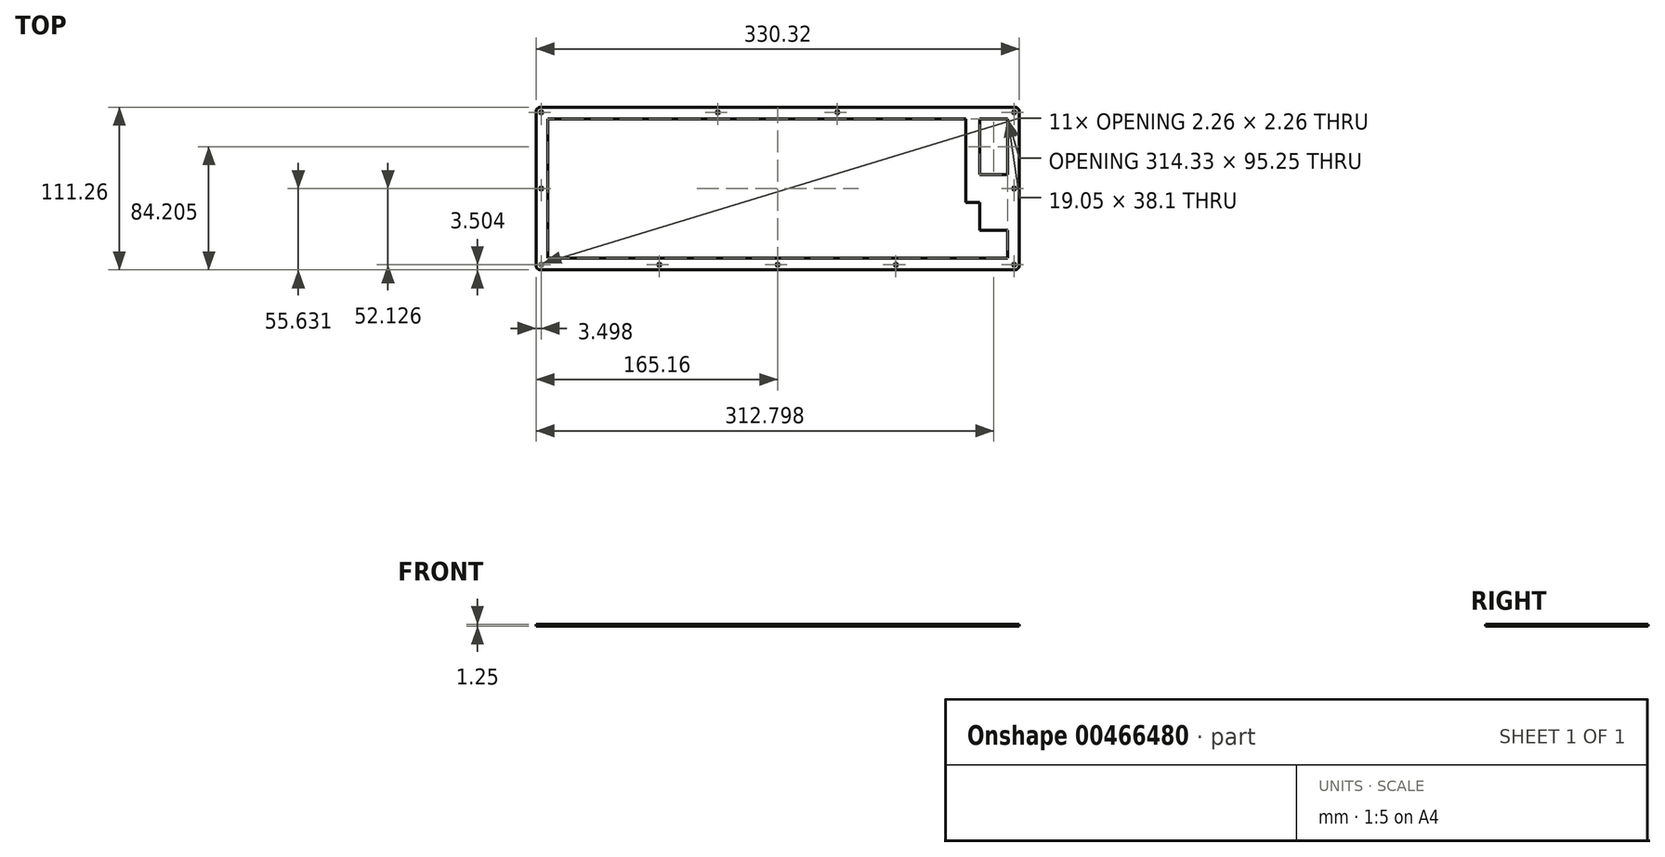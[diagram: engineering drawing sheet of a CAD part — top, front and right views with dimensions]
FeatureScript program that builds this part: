
annotation { "Feature Type Name" : "Feature", "Feature Type Description" : "" }
export const myFeature = defineFeature(function(context is Context, id is Id, definition is map)
    precondition{}
    {
        {
            var Q0;
            Q0=qCreatedBy(makeId("Top.planeOp"),FACE);
            var sketch = newSketch(context, id + "F0", { "sketchPlane" : qUnion([Q0])});
            skLineSegment(sketch, "E0", {"start": v(162.16, 55.62) * mm, "end": v(162.4, 55.62) * mm});
            skLineSegment(sketch, "E1", {"start": v(162.4, 55.62) * mm, "end": v(162.63, 55.59) * mm});
            skLineSegment(sketch, "E2", {"start": v(162.63, 55.59) * mm, "end": v(162.86, 55.54) * mm});
            skLineSegment(sketch, "E3", {"start": v(162.86, 55.54) * mm, "end": v(163.1, 55.48) * mm});
            skLineSegment(sketch, "E4", {"start": v(163.1, 55.48) * mm, "end": v(163.31, 55.4) * mm});
            skLineSegment(sketch, "E5", {"start": v(163.31, 55.4) * mm, "end": v(163.53, 55.3) * mm});
            skLineSegment(sketch, "E6", {"start": v(163.53, 55.3) * mm, "end": v(163.73, 55.18) * mm});
            skLineSegment(sketch, "E7", {"start": v(163.73, 55.18) * mm, "end": v(163.93, 55.05) * mm});
            skLineSegment(sketch, "E8", {"start": v(163.93, 55.05) * mm, "end": v(164.11, 54.9) * mm});
            skLineSegment(sketch, "E9", {"start": v(164.11, 54.9) * mm, "end": v(164.29, 54.75) * mm});
            skLineSegment(sketch, "E10", {"start": v(164.29, 54.75) * mm, "end": v(164.45, 54.57) * mm});
            skLineSegment(sketch, "E11", {"start": v(164.45, 54.57) * mm, "end": v(164.6, 54.39) * mm});
            skLineSegment(sketch, "E12", {"start": v(164.6, 54.39) * mm, "end": v(164.72, 54.2) * mm});
            skLineSegment(sketch, "E13", {"start": v(164.72, 54.2) * mm, "end": v(164.84, 53.99) * mm});
            skLineSegment(sketch, "E14", {"start": v(164.84, 53.99) * mm, "end": v(164.93, 53.77) * mm});
            skLineSegment(sketch, "E15", {"start": v(164.93, 53.77) * mm, "end": v(165.02, 53.55) * mm});
            skLineSegment(sketch, "E16", {"start": v(165.02, 53.55) * mm, "end": v(165.08, 53.33) * mm});
            skLineSegment(sketch, "E17", {"start": v(165.08, 53.33) * mm, "end": v(165.13, 53.1) * mm});
            skLineSegment(sketch, "E18", {"start": v(165.13, 53.1) * mm, "end": v(165.15, 52.86) * mm});
            skLineSegment(sketch, "E19", {"start": v(165.15, 52.86) * mm, "end": v(165.16, 52.62) * mm});
            skLineSegment(sketch, "E20", {"start": v(165.16, 52.62) * mm, "end": v(165.16, -52.63) * mm});
            skLineSegment(sketch, "E21", {"start": v(165.16, -52.63) * mm, "end": v(165.15, -52.86) * mm});
            skLineSegment(sketch, "E22", {"start": v(165.15, -52.86) * mm, "end": v(165.13, -53.1) * mm});
            skLineSegment(sketch, "E23", {"start": v(165.13, -53.1) * mm, "end": v(165.08, -53.33) * mm});
            skLineSegment(sketch, "E24", {"start": v(165.08, -53.33) * mm, "end": v(165.02, -53.55) * mm});
            skLineSegment(sketch, "E25", {"start": v(165.02, -53.55) * mm, "end": v(164.93, -53.77) * mm});
            skLineSegment(sketch, "E26", {"start": v(164.93, -53.77) * mm, "end": v(164.84, -53.99) * mm});
            skLineSegment(sketch, "E27", {"start": v(164.84, -53.99) * mm, "end": v(164.72, -54.2) * mm});
            skLineSegment(sketch, "E28", {"start": v(164.72, -54.2) * mm, "end": v(164.6, -54.39) * mm});
            skLineSegment(sketch, "E29", {"start": v(164.6, -54.39) * mm, "end": v(164.45, -54.57) * mm});
            skLineSegment(sketch, "E30", {"start": v(164.45, -54.57) * mm, "end": v(164.29, -54.75) * mm});
            skLineSegment(sketch, "E31", {"start": v(164.29, -54.75) * mm, "end": v(164.11, -54.9) * mm});
            skLineSegment(sketch, "E32", {"start": v(164.11, -54.9) * mm, "end": v(163.93, -55.05) * mm});
            skLineSegment(sketch, "E33", {"start": v(163.93, -55.05) * mm, "end": v(163.73, -55.18) * mm});
            skLineSegment(sketch, "E34", {"start": v(163.73, -55.18) * mm, "end": v(163.53, -55.3) * mm});
            skLineSegment(sketch, "E35", {"start": v(163.53, -55.3) * mm, "end": v(163.31, -55.4) * mm});
            skLineSegment(sketch, "E36", {"start": v(163.31, -55.4) * mm, "end": v(163.1, -55.48) * mm});
            skLineSegment(sketch, "E37", {"start": v(163.1, -55.48) * mm, "end": v(162.86, -55.54) * mm});
            skLineSegment(sketch, "E38", {"start": v(162.86, -55.54) * mm, "end": v(162.63, -55.59) * mm});
            skLineSegment(sketch, "E39", {"start": v(162.63, -55.59) * mm, "end": v(162.4, -55.62) * mm});
            skLineSegment(sketch, "E40", {"start": v(162.4, -55.62) * mm, "end": v(162.16, -55.63) * mm});
            skLineSegment(sketch, "E41", {"start": v(162.16, -55.63) * mm, "end": v(-162.16, -55.63) * mm});
            skLineSegment(sketch, "E42", {"start": v(-162.16, -55.63) * mm, "end": v(-162.4, -55.62) * mm});
            skLineSegment(sketch, "E43", {"start": v(-162.4, -55.62) * mm, "end": v(-162.63, -55.59) * mm});
            skLineSegment(sketch, "E44", {"start": v(-162.63, -55.59) * mm, "end": v(-162.86, -55.54) * mm});
            skLineSegment(sketch, "E45", {"start": v(-162.86, -55.54) * mm, "end": v(-163.09, -55.48) * mm});
            skLineSegment(sketch, "E46", {"start": v(-163.09, -55.48) * mm, "end": v(-163.31, -55.4) * mm});
            skLineSegment(sketch, "E47", {"start": v(-163.31, -55.4) * mm, "end": v(-163.52, -55.3) * mm});
            skLineSegment(sketch, "E48", {"start": v(-163.52, -55.3) * mm, "end": v(-163.73, -55.18) * mm});
            skLineSegment(sketch, "E49", {"start": v(-163.73, -55.18) * mm, "end": v(-163.93, -55.05) * mm});
            skLineSegment(sketch, "E50", {"start": v(-163.93, -55.05) * mm, "end": v(-164.11, -54.9) * mm});
            skLineSegment(sketch, "E51", {"start": v(-164.11, -54.9) * mm, "end": v(-164.28, -54.75) * mm});
            skLineSegment(sketch, "E52", {"start": v(-164.28, -54.75) * mm, "end": v(-164.44, -54.57) * mm});
            skLineSegment(sketch, "E53", {"start": v(-164.44, -54.57) * mm, "end": v(-164.6, -54.39) * mm});
            skLineSegment(sketch, "E54", {"start": v(-164.6, -54.39) * mm, "end": v(-164.72, -54.2) * mm});
            skLineSegment(sketch, "E55", {"start": v(-164.72, -54.2) * mm, "end": v(-164.84, -53.99) * mm});
            skLineSegment(sketch, "E56", {"start": v(-164.84, -53.99) * mm, "end": v(-164.93, -53.77) * mm});
            skLineSegment(sketch, "E57", {"start": v(-164.93, -53.77) * mm, "end": v(-165.02, -53.55) * mm});
            skLineSegment(sketch, "E58", {"start": v(-165.02, -53.55) * mm, "end": v(-165.08, -53.33) * mm});
            skLineSegment(sketch, "E59", {"start": v(-165.08, -53.33) * mm, "end": v(-165.13, -53.1) * mm});
            skLineSegment(sketch, "E60", {"start": v(-165.13, -53.1) * mm, "end": v(-165.15, -52.86) * mm});
            skLineSegment(sketch, "E61", {"start": v(-165.15, -52.86) * mm, "end": v(-165.16, -52.63) * mm});
            skLineSegment(sketch, "E62", {"start": v(-165.16, -52.63) * mm, "end": v(-165.16, 52.62) * mm});
            skLineSegment(sketch, "E63", {"start": v(-165.16, 52.62) * mm, "end": v(-165.15, 52.86) * mm});
            skLineSegment(sketch, "E64", {"start": v(-165.15, 52.86) * mm, "end": v(-165.13, 53.1) * mm});
            skLineSegment(sketch, "E65", {"start": v(-165.13, 53.1) * mm, "end": v(-165.08, 53.33) * mm});
            skLineSegment(sketch, "E66", {"start": v(-165.08, 53.33) * mm, "end": v(-165.02, 53.55) * mm});
            skLineSegment(sketch, "E67", {"start": v(-165.02, 53.55) * mm, "end": v(-164.93, 53.77) * mm});
            skLineSegment(sketch, "E68", {"start": v(-164.93, 53.77) * mm, "end": v(-164.84, 53.99) * mm});
            skLineSegment(sketch, "E69", {"start": v(-164.84, 53.99) * mm, "end": v(-164.72, 54.2) * mm});
            skLineSegment(sketch, "E70", {"start": v(-164.72, 54.2) * mm, "end": v(-164.6, 54.39) * mm});
            skLineSegment(sketch, "E71", {"start": v(-164.6, 54.39) * mm, "end": v(-164.44, 54.57) * mm});
            skLineSegment(sketch, "E72", {"start": v(-164.44, 54.57) * mm, "end": v(-164.28, 54.75) * mm});
            skLineSegment(sketch, "E73", {"start": v(-164.28, 54.75) * mm, "end": v(-164.11, 54.9) * mm});
            skLineSegment(sketch, "E74", {"start": v(-164.11, 54.9) * mm, "end": v(-163.93, 55.05) * mm});
            skLineSegment(sketch, "E75", {"start": v(-163.93, 55.05) * mm, "end": v(-163.73, 55.18) * mm});
            skLineSegment(sketch, "E76", {"start": v(-163.73, 55.18) * mm, "end": v(-163.52, 55.3) * mm});
            skLineSegment(sketch, "E77", {"start": v(-163.52, 55.3) * mm, "end": v(-163.31, 55.4) * mm});
            skLineSegment(sketch, "E78", {"start": v(-163.31, 55.4) * mm, "end": v(-163.09, 55.48) * mm});
            skLineSegment(sketch, "E79", {"start": v(-163.09, 55.48) * mm, "end": v(-162.86, 55.54) * mm});
            skLineSegment(sketch, "E80", {"start": v(-162.86, 55.54) * mm, "end": v(-162.63, 55.59) * mm});
            skLineSegment(sketch, "E81", {"start": v(-162.63, 55.59) * mm, "end": v(-162.4, 55.62) * mm});
            skLineSegment(sketch, "E82", {"start": v(-162.4, 55.62) * mm, "end": v(-162.16, 55.63) * mm});
            skLineSegment(sketch, "E83", {"start": v(-162.16, 55.63) * mm, "end": v(162.16, 55.62) * mm});
            skLineSegment(sketch, "E84", {"start": v(161.31, -51.05) * mm, "end": v(161, -51.21) * mm});
            skLineSegment(sketch, "E85", {"start": v(161, -51.21) * mm, "end": v(160.75, -51.46) * mm});
            skLineSegment(sketch, "E86", {"start": v(160.75, -51.46) * mm, "end": v(160.59, -51.78) * mm});
            skLineSegment(sketch, "E87", {"start": v(160.59, -51.78) * mm, "end": v(160.53, -52.13) * mm});
            skLineSegment(sketch, "E88", {"start": v(160.53, -52.13) * mm, "end": v(160.59, -52.48) * mm});
            skLineSegment(sketch, "E89", {"start": v(160.59, -52.48) * mm, "end": v(160.75, -52.79) * mm});
            skLineSegment(sketch, "E90", {"start": v(160.75, -52.79) * mm, "end": v(161, -53.04) * mm});
            skLineSegment(sketch, "E91", {"start": v(161, -53.04) * mm, "end": v(161.31, -53.2) * mm});
            skLineSegment(sketch, "E92", {"start": v(161.31, -53.2) * mm, "end": v(161.66, -53.26) * mm});
            skLineSegment(sketch, "E93", {"start": v(161.66, -53.26) * mm, "end": v(162.01, -53.2) * mm});
            skLineSegment(sketch, "E94", {"start": v(162.01, -53.2) * mm, "end": v(162.33, -53.04) * mm});
            skLineSegment(sketch, "E95", {"start": v(162.33, -53.04) * mm, "end": v(162.58, -52.79) * mm});
            skLineSegment(sketch, "E96", {"start": v(162.58, -52.79) * mm, "end": v(162.74, -52.48) * mm});
            skLineSegment(sketch, "E97", {"start": v(162.74, -52.48) * mm, "end": v(162.8, -52.13) * mm});
            skLineSegment(sketch, "E98", {"start": v(162.8, -52.13) * mm, "end": v(162.74, -51.78) * mm});
            skLineSegment(sketch, "E99", {"start": v(162.74, -51.78) * mm, "end": v(162.58, -51.46) * mm});
            skLineSegment(sketch, "E100", {"start": v(162.58, -51.46) * mm, "end": v(162.33, -51.21) * mm});
            skLineSegment(sketch, "E101", {"start": v(162.33, -51.21) * mm, "end": v(162.01, -51.05) * mm});
            skLineSegment(sketch, "E102", {"start": v(162.01, -51.05) * mm, "end": v(161.66, -51) * mm});
            skLineSegment(sketch, "E103", {"start": v(161.66, -51) * mm, "end": v(161.31, -51.05) * mm});
            skLineSegment(sketch, "E104", {"start": v(80.48, -51.05) * mm, "end": v(80.17, -51.21) * mm});
            skLineSegment(sketch, "E105", {"start": v(80.17, -51.21) * mm, "end": v(79.92, -51.46) * mm});
            skLineSegment(sketch, "E106", {"start": v(79.92, -51.46) * mm, "end": v(79.76, -51.78) * mm});
            skLineSegment(sketch, "E107", {"start": v(79.76, -51.78) * mm, "end": v(79.7, -52.13) * mm});
            skLineSegment(sketch, "E108", {"start": v(79.7, -52.13) * mm, "end": v(79.76, -52.48) * mm});
            skLineSegment(sketch, "E109", {"start": v(79.76, -52.48) * mm, "end": v(79.92, -52.79) * mm});
            skLineSegment(sketch, "E110", {"start": v(79.92, -52.79) * mm, "end": v(80.17, -53.04) * mm});
            skLineSegment(sketch, "E111", {"start": v(80.17, -53.04) * mm, "end": v(80.48, -53.2) * mm});
            skLineSegment(sketch, "E112", {"start": v(80.48, -53.2) * mm, "end": v(80.83, -53.26) * mm});
            skLineSegment(sketch, "E113", {"start": v(80.83, -53.26) * mm, "end": v(81.18, -53.2) * mm});
            skLineSegment(sketch, "E114", {"start": v(81.18, -53.2) * mm, "end": v(81.5, -53.04) * mm});
            skLineSegment(sketch, "E115", {"start": v(81.5, -53.04) * mm, "end": v(81.75, -52.79) * mm});
            skLineSegment(sketch, "E116", {"start": v(81.75, -52.79) * mm, "end": v(81.9, -52.48) * mm});
            skLineSegment(sketch, "E117", {"start": v(81.9, -52.48) * mm, "end": v(81.96, -52.13) * mm});
            skLineSegment(sketch, "E118", {"start": v(81.96, -52.13) * mm, "end": v(81.9, -51.78) * mm});
            skLineSegment(sketch, "E119", {"start": v(81.9, -51.78) * mm, "end": v(81.75, -51.46) * mm});
            skLineSegment(sketch, "E120", {"start": v(81.75, -51.46) * mm, "end": v(81.5, -51.21) * mm});
            skLineSegment(sketch, "E121", {"start": v(81.5, -51.21) * mm, "end": v(81.18, -51.05) * mm});
            skLineSegment(sketch, "E122", {"start": v(81.18, -51.05) * mm, "end": v(80.83, -51) * mm});
            skLineSegment(sketch, "E123", {"start": v(80.83, -51) * mm, "end": v(80.48, -51.05) * mm});
            skLineSegment(sketch, "E124", {"start": v(-0.35, -51.05) * mm, "end": v(-0.66, -51.21) * mm});
            skLineSegment(sketch, "E125", {"start": v(-0.66, -51.21) * mm, "end": v(-0.91, -51.46) * mm});
            skLineSegment(sketch, "E126", {"start": v(-0.91, -51.46) * mm, "end": v(-1.07, -51.78) * mm});
            skLineSegment(sketch, "E127", {"start": v(-1.07, -51.78) * mm, "end": v(-1.13, -52.13) * mm});
            skLineSegment(sketch, "E128", {"start": v(-1.13, -52.13) * mm, "end": v(-1.07, -52.48) * mm});
            skLineSegment(sketch, "E129", {"start": v(-1.07, -52.48) * mm, "end": v(-0.91, -52.79) * mm});
            skLineSegment(sketch, "E130", {"start": v(-0.91, -52.79) * mm, "end": v(-0.66, -53.04) * mm});
            skLineSegment(sketch, "E131", {"start": v(-0.66, -53.04) * mm, "end": v(-0.35, -53.2) * mm});
            skLineSegment(sketch, "E132", {"start": v(-0.35, -53.2) * mm, "end": v(0, -53.26) * mm});
            skLineSegment(sketch, "E133", {"start": v(0, -53.26) * mm, "end": v(0.35, -53.2) * mm});
            skLineSegment(sketch, "E134", {"start": v(0.35, -53.2) * mm, "end": v(0.67, -53.04) * mm});
            skLineSegment(sketch, "E135", {"start": v(0.67, -53.04) * mm, "end": v(0.92, -52.79) * mm});
            skLineSegment(sketch, "E136", {"start": v(0.92, -52.79) * mm, "end": v(1.07, -52.48) * mm});
            skLineSegment(sketch, "E137", {"start": v(1.07, -52.48) * mm, "end": v(1.13, -52.13) * mm});
            skLineSegment(sketch, "E138", {"start": v(1.13, -52.13) * mm, "end": v(1.07, -51.78) * mm});
            skLineSegment(sketch, "E139", {"start": v(1.07, -51.78) * mm, "end": v(0.92, -51.46) * mm});
            skLineSegment(sketch, "E140", {"start": v(0.92, -51.46) * mm, "end": v(0.67, -51.21) * mm});
            skLineSegment(sketch, "E141", {"start": v(0.67, -51.21) * mm, "end": v(0.35, -51.05) * mm});
            skLineSegment(sketch, "E142", {"start": v(0.35, -51.05) * mm, "end": v(0, -51) * mm});
            skLineSegment(sketch, "E143", {"start": v(0, -51) * mm, "end": v(-0.35, -51.05) * mm});
            skLineSegment(sketch, "E144", {"start": v(-81.18, -51.05) * mm, "end": v(-81.5, -51.21) * mm});
            skLineSegment(sketch, "E145", {"start": v(-81.5, -51.21) * mm, "end": v(-81.75, -51.46) * mm});
            skLineSegment(sketch, "E146", {"start": v(-81.75, -51.46) * mm, "end": v(-81.9, -51.78) * mm});
            skLineSegment(sketch, "E147", {"start": v(-81.9, -51.78) * mm, "end": v(-81.96, -52.13) * mm});
            skLineSegment(sketch, "E148", {"start": v(-81.96, -52.13) * mm, "end": v(-81.9, -52.48) * mm});
            skLineSegment(sketch, "E149", {"start": v(-81.9, -52.48) * mm, "end": v(-81.75, -52.79) * mm});
            skLineSegment(sketch, "E150", {"start": v(-81.75, -52.79) * mm, "end": v(-81.5, -53.04) * mm});
            skLineSegment(sketch, "E151", {"start": v(-81.5, -53.04) * mm, "end": v(-81.18, -53.2) * mm});
            skLineSegment(sketch, "E152", {"start": v(-81.18, -53.2) * mm, "end": v(-80.83, -53.26) * mm});
            skLineSegment(sketch, "E153", {"start": v(-80.83, -53.26) * mm, "end": v(-80.48, -53.2) * mm});
            skLineSegment(sketch, "E154", {"start": v(-80.48, -53.2) * mm, "end": v(-80.17, -53.04) * mm});
            skLineSegment(sketch, "E155", {"start": v(-80.17, -53.04) * mm, "end": v(-79.92, -52.79) * mm});
            skLineSegment(sketch, "E156", {"start": v(-79.92, -52.79) * mm, "end": v(-79.76, -52.48) * mm});
            skLineSegment(sketch, "E157", {"start": v(-79.76, -52.48) * mm, "end": v(-79.7, -52.13) * mm});
            skLineSegment(sketch, "E158", {"start": v(-79.7, -52.13) * mm, "end": v(-79.76, -51.78) * mm});
            skLineSegment(sketch, "E159", {"start": v(-79.76, -51.78) * mm, "end": v(-79.92, -51.46) * mm});
            skLineSegment(sketch, "E160", {"start": v(-79.92, -51.46) * mm, "end": v(-80.17, -51.21) * mm});
            skLineSegment(sketch, "E161", {"start": v(-80.17, -51.21) * mm, "end": v(-80.48, -51.05) * mm});
            skLineSegment(sketch, "E162", {"start": v(-80.48, -51.05) * mm, "end": v(-80.83, -51) * mm});
            skLineSegment(sketch, "E163", {"start": v(-80.83, -51) * mm, "end": v(-81.18, -51.05) * mm});
            skLineSegment(sketch, "E164", {"start": v(-162.01, -51.05) * mm, "end": v(-162.33, -51.21) * mm});
            skLineSegment(sketch, "E165", {"start": v(-162.33, -51.21) * mm, "end": v(-162.58, -51.46) * mm});
            skLineSegment(sketch, "E166", {"start": v(-162.58, -51.46) * mm, "end": v(-162.74, -51.78) * mm});
            skLineSegment(sketch, "E167", {"start": v(-162.74, -51.78) * mm, "end": v(-162.8, -52.13) * mm});
            skLineSegment(sketch, "E168", {"start": v(-162.8, -52.13) * mm, "end": v(-162.74, -52.48) * mm});
            skLineSegment(sketch, "E169", {"start": v(-162.74, -52.48) * mm, "end": v(-162.58, -52.79) * mm});
            skLineSegment(sketch, "E170", {"start": v(-162.58, -52.79) * mm, "end": v(-162.33, -53.04) * mm});
            skLineSegment(sketch, "E171", {"start": v(-162.33, -53.04) * mm, "end": v(-162.01, -53.2) * mm});
            skLineSegment(sketch, "E172", {"start": v(-162.01, -53.2) * mm, "end": v(-161.66, -53.26) * mm});
            skLineSegment(sketch, "E173", {"start": v(-161.66, -53.26) * mm, "end": v(-161.31, -53.2) * mm});
            skLineSegment(sketch, "E174", {"start": v(-161.31, -53.2) * mm, "end": v(-161, -53.04) * mm});
            skLineSegment(sketch, "E175", {"start": v(-161, -53.04) * mm, "end": v(-160.75, -52.79) * mm});
            skLineSegment(sketch, "E176", {"start": v(-160.75, -52.79) * mm, "end": v(-160.59, -52.48) * mm});
            skLineSegment(sketch, "E177", {"start": v(-160.59, -52.48) * mm, "end": v(-160.53, -52.13) * mm});
            skLineSegment(sketch, "E178", {"start": v(-160.53, -52.13) * mm, "end": v(-160.59, -51.78) * mm});
            skLineSegment(sketch, "E179", {"start": v(-160.59, -51.78) * mm, "end": v(-160.75, -51.46) * mm});
            skLineSegment(sketch, "E180", {"start": v(-160.75, -51.46) * mm, "end": v(-161, -51.21) * mm});
            skLineSegment(sketch, "E181", {"start": v(-161, -51.21) * mm, "end": v(-161.31, -51.05) * mm});
            skLineSegment(sketch, "E182", {"start": v(-161.31, -51.05) * mm, "end": v(-161.66, -51) * mm});
            skLineSegment(sketch, "E183", {"start": v(-161.66, -51) * mm, "end": v(-162.01, -51.05) * mm});
            skLineSegment(sketch, "E184", {"start": v(-157.16, 47.63) * mm, "end": v(-157.16, 28.57) * mm});
            skLineSegment(sketch, "E185", {"start": v(-157.16, 28.57) * mm, "end": v(-157.16, 28.57) * mm});
            skLineSegment(sketch, "E186", {"start": v(-157.16, 28.57) * mm, "end": v(-157.16, 9.53) * mm});
            skLineSegment(sketch, "E187", {"start": v(-157.16, 9.53) * mm, "end": v(-157.16, 9.53) * mm});
            skLineSegment(sketch, "E188", {"start": v(-157.16, 9.53) * mm, "end": v(-157.16, -9.53) * mm});
            skLineSegment(sketch, "E189", {"start": v(-157.16, -9.53) * mm, "end": v(-157.16, -9.53) * mm});
            skLineSegment(sketch, "E190", {"start": v(-157.16, -9.53) * mm, "end": v(-157.16, -47.62) * mm});
            skLineSegment(sketch, "E191", {"start": v(-157.16, -47.62) * mm, "end": v(157.16, -47.62) * mm});
            skLineSegment(sketch, "E192", {"start": v(157.16, -47.62) * mm, "end": v(157.16, -28.57) * mm});
            skLineSegment(sketch, "E193", {"start": v(157.16, -28.57) * mm, "end": v(138.11, -28.57) * mm});
            skLineSegment(sketch, "E194", {"start": v(138.11, -28.57) * mm, "end": v(138.11, -9.52) * mm});
            skLineSegment(sketch, "E195", {"start": v(138.11, -9.52) * mm, "end": v(128.59, -9.52) * mm});
            skLineSegment(sketch, "E196", {"start": v(128.59, -9.52) * mm, "end": v(128.59, 47.63) * mm});
            skLineSegment(sketch, "E197", {"start": v(128.59, 47.63) * mm, "end": v(-157.16, 47.63) * mm});
            skLineSegment(sketch, "E198", {"start": v(161.31, 1.08) * mm, "end": v(161, 0.91) * mm});
            skLineSegment(sketch, "E199", {"start": v(161, 0.91) * mm, "end": v(160.75, 0.66) * mm});
            skLineSegment(sketch, "E200", {"start": v(160.75, 0.66) * mm, "end": v(160.59, 0.35) * mm});
            skLineSegment(sketch, "E201", {"start": v(160.59, 0.35) * mm, "end": v(160.53, 0) * mm});
            skLineSegment(sketch, "E202", {"start": v(160.53, 0) * mm, "end": v(160.59, -0.35) * mm});
            skLineSegment(sketch, "E203", {"start": v(160.59, -0.35) * mm, "end": v(160.75, -0.66) * mm});
            skLineSegment(sketch, "E204", {"start": v(160.75, -0.66) * mm, "end": v(161, -0.91) * mm});
            skLineSegment(sketch, "E205", {"start": v(161, -0.91) * mm, "end": v(161.31, -1.07) * mm});
            skLineSegment(sketch, "E206", {"start": v(161.31, -1.07) * mm, "end": v(161.66, -1.13) * mm});
            skLineSegment(sketch, "E207", {"start": v(161.66, -1.13) * mm, "end": v(162.01, -1.07) * mm});
            skLineSegment(sketch, "E208", {"start": v(162.01, -1.07) * mm, "end": v(162.33, -0.91) * mm});
            skLineSegment(sketch, "E209", {"start": v(162.33, -0.91) * mm, "end": v(162.58, -0.66) * mm});
            skLineSegment(sketch, "E210", {"start": v(162.58, -0.66) * mm, "end": v(162.74, -0.35) * mm});
            skLineSegment(sketch, "E211", {"start": v(162.74, -0.35) * mm, "end": v(162.8, 0) * mm});
            skLineSegment(sketch, "E212", {"start": v(162.8, 0) * mm, "end": v(162.74, 0.35) * mm});
            skLineSegment(sketch, "E213", {"start": v(162.74, 0.35) * mm, "end": v(162.58, 0.66) * mm});
            skLineSegment(sketch, "E214", {"start": v(162.58, 0.66) * mm, "end": v(162.33, 0.91) * mm});
            skLineSegment(sketch, "E215", {"start": v(162.33, 0.91) * mm, "end": v(162.01, 1.08) * mm});
            skLineSegment(sketch, "E216", {"start": v(162.01, 1.08) * mm, "end": v(161.66, 1.13) * mm});
            skLineSegment(sketch, "E217", {"start": v(161.66, 1.13) * mm, "end": v(161.31, 1.08) * mm});
            skLineSegment(sketch, "E218", {"start": v(-162.01, 1.08) * mm, "end": v(-162.33, 0.91) * mm});
            skLineSegment(sketch, "E219", {"start": v(-162.33, 0.91) * mm, "end": v(-162.58, 0.66) * mm});
            skLineSegment(sketch, "E220", {"start": v(-162.58, 0.66) * mm, "end": v(-162.74, 0.35) * mm});
            skLineSegment(sketch, "E221", {"start": v(-162.74, 0.35) * mm, "end": v(-162.8, 0) * mm});
            skLineSegment(sketch, "E222", {"start": v(-162.8, 0) * mm, "end": v(-162.74, -0.35) * mm});
            skLineSegment(sketch, "E223", {"start": v(-162.74, -0.35) * mm, "end": v(-162.58, -0.66) * mm});
            skLineSegment(sketch, "E224", {"start": v(-162.58, -0.66) * mm, "end": v(-162.33, -0.91) * mm});
            skLineSegment(sketch, "E225", {"start": v(-162.33, -0.91) * mm, "end": v(-162.01, -1.07) * mm});
            skLineSegment(sketch, "E226", {"start": v(-162.01, -1.07) * mm, "end": v(-161.66, -1.13) * mm});
            skLineSegment(sketch, "E227", {"start": v(-161.66, -1.13) * mm, "end": v(-161.31, -1.07) * mm});
            skLineSegment(sketch, "E228", {"start": v(-161.31, -1.07) * mm, "end": v(-161, -0.91) * mm});
            skLineSegment(sketch, "E229", {"start": v(-161, -0.91) * mm, "end": v(-160.75, -0.66) * mm});
            skLineSegment(sketch, "E230", {"start": v(-160.75, -0.66) * mm, "end": v(-160.59, -0.35) * mm});
            skLineSegment(sketch, "E231", {"start": v(-160.59, -0.35) * mm, "end": v(-160.53, 0) * mm});
            skLineSegment(sketch, "E232", {"start": v(-160.53, 0) * mm, "end": v(-160.59, 0.35) * mm});
            skLineSegment(sketch, "E233", {"start": v(-160.59, 0.35) * mm, "end": v(-160.75, 0.66) * mm});
            skLineSegment(sketch, "E234", {"start": v(-160.75, 0.66) * mm, "end": v(-161, 0.91) * mm});
            skLineSegment(sketch, "E235", {"start": v(-161, 0.91) * mm, "end": v(-161.31, 1.08) * mm});
            skLineSegment(sketch, "E236", {"start": v(-161.31, 1.08) * mm, "end": v(-161.66, 1.13) * mm});
            skLineSegment(sketch, "E237", {"start": v(-161.66, 1.13) * mm, "end": v(-162.01, 1.08) * mm});
            skLineSegment(sketch, "E238", {"start": v(138.11, 47.63) * mm, "end": v(157.16, 47.63) * mm});
            skLineSegment(sketch, "E239", {"start": v(157.16, 47.63) * mm, "end": v(157.16, 9.52) * mm});
            skLineSegment(sketch, "E240", {"start": v(157.16, 9.52) * mm, "end": v(138.11, 9.52) * mm});
            skLineSegment(sketch, "E241", {"start": v(138.11, 9.52) * mm, "end": v(138.11, 47.63) * mm});
            skLineSegment(sketch, "E242", {"start": v(-41.18, 53.2) * mm, "end": v(-41.5, 53.04) * mm});
            skLineSegment(sketch, "E243", {"start": v(-41.5, 53.04) * mm, "end": v(-41.75, 52.8) * mm});
            skLineSegment(sketch, "E244", {"start": v(-41.75, 52.8) * mm, "end": v(-41.9, 52.47) * mm});
            skLineSegment(sketch, "E245", {"start": v(-41.9, 52.47) * mm, "end": v(-41.96, 52.12) * mm});
            skLineSegment(sketch, "E246", {"start": v(-41.96, 52.12) * mm, "end": v(-41.9, 51.78) * mm});
            skLineSegment(sketch, "E247", {"start": v(-41.9, 51.78) * mm, "end": v(-41.75, 51.46) * mm});
            skLineSegment(sketch, "E248", {"start": v(-41.75, 51.46) * mm, "end": v(-41.5, 51.21) * mm});
            skLineSegment(sketch, "E249", {"start": v(-41.5, 51.21) * mm, "end": v(-41.18, 51.05) * mm});
            skLineSegment(sketch, "E250", {"start": v(-41.18, 51.05) * mm, "end": v(-40.83, 51) * mm});
            skLineSegment(sketch, "E251", {"start": v(-40.83, 51) * mm, "end": v(-40.48, 51.05) * mm});
            skLineSegment(sketch, "E252", {"start": v(-40.48, 51.05) * mm, "end": v(-40.17, 51.21) * mm});
            skLineSegment(sketch, "E253", {"start": v(-40.17, 51.21) * mm, "end": v(-39.92, 51.46) * mm});
            skLineSegment(sketch, "E254", {"start": v(-39.92, 51.46) * mm, "end": v(-39.76, 51.78) * mm});
            skLineSegment(sketch, "E255", {"start": v(-39.76, 51.78) * mm, "end": v(-39.7, 52.12) * mm});
            skLineSegment(sketch, "E256", {"start": v(-39.7, 52.12) * mm, "end": v(-39.76, 52.47) * mm});
            skLineSegment(sketch, "E257", {"start": v(-39.76, 52.47) * mm, "end": v(-39.92, 52.8) * mm});
            skLineSegment(sketch, "E258", {"start": v(-39.92, 52.8) * mm, "end": v(-40.17, 53.04) * mm});
            skLineSegment(sketch, "E259", {"start": v(-40.17, 53.04) * mm, "end": v(-40.48, 53.2) * mm});
            skLineSegment(sketch, "E260", {"start": v(-40.48, 53.2) * mm, "end": v(-40.83, 53.26) * mm});
            skLineSegment(sketch, "E261", {"start": v(-40.83, 53.26) * mm, "end": v(-41.18, 53.2) * mm});
            skLineSegment(sketch, "E262", {"start": v(40.48, 53.2) * mm, "end": v(40.17, 53.04) * mm});
            skLineSegment(sketch, "E263", {"start": v(40.17, 53.04) * mm, "end": v(39.92, 52.8) * mm});
            skLineSegment(sketch, "E264", {"start": v(39.92, 52.8) * mm, "end": v(39.76, 52.47) * mm});
            skLineSegment(sketch, "E265", {"start": v(39.76, 52.47) * mm, "end": v(39.7, 52.12) * mm});
            skLineSegment(sketch, "E266", {"start": v(39.7, 52.12) * mm, "end": v(39.76, 51.78) * mm});
            skLineSegment(sketch, "E267", {"start": v(39.76, 51.78) * mm, "end": v(39.92, 51.46) * mm});
            skLineSegment(sketch, "E268", {"start": v(39.92, 51.46) * mm, "end": v(40.17, 51.21) * mm});
            skLineSegment(sketch, "E269", {"start": v(40.17, 51.21) * mm, "end": v(40.48, 51.05) * mm});
            skLineSegment(sketch, "E270", {"start": v(40.48, 51.05) * mm, "end": v(40.83, 51) * mm});
            skLineSegment(sketch, "E271", {"start": v(40.83, 51) * mm, "end": v(41.18, 51.05) * mm});
            skLineSegment(sketch, "E272", {"start": v(41.18, 51.05) * mm, "end": v(41.5, 51.21) * mm});
            skLineSegment(sketch, "E273", {"start": v(41.5, 51.21) * mm, "end": v(41.75, 51.46) * mm});
            skLineSegment(sketch, "E274", {"start": v(41.75, 51.46) * mm, "end": v(41.9, 51.78) * mm});
            skLineSegment(sketch, "E275", {"start": v(41.9, 51.78) * mm, "end": v(41.96, 52.12) * mm});
            skLineSegment(sketch, "E276", {"start": v(41.96, 52.12) * mm, "end": v(41.9, 52.47) * mm});
            skLineSegment(sketch, "E277", {"start": v(41.9, 52.47) * mm, "end": v(41.75, 52.8) * mm});
            skLineSegment(sketch, "E278", {"start": v(41.75, 52.8) * mm, "end": v(41.5, 53.04) * mm});
            skLineSegment(sketch, "E279", {"start": v(41.5, 53.04) * mm, "end": v(41.18, 53.2) * mm});
            skLineSegment(sketch, "E280", {"start": v(41.18, 53.2) * mm, "end": v(40.83, 53.26) * mm});
            skLineSegment(sketch, "E281", {"start": v(40.83, 53.26) * mm, "end": v(40.48, 53.2) * mm});
            skLineSegment(sketch, "E282", {"start": v(161.31, 53.2) * mm, "end": v(161, 53.04) * mm});
            skLineSegment(sketch, "E283", {"start": v(161, 53.04) * mm, "end": v(160.75, 52.8) * mm});
            skLineSegment(sketch, "E284", {"start": v(160.75, 52.8) * mm, "end": v(160.59, 52.47) * mm});
            skLineSegment(sketch, "E285", {"start": v(160.59, 52.47) * mm, "end": v(160.53, 52.12) * mm});
            skLineSegment(sketch, "E286", {"start": v(160.53, 52.12) * mm, "end": v(160.59, 51.78) * mm});
            skLineSegment(sketch, "E287", {"start": v(160.59, 51.78) * mm, "end": v(160.75, 51.46) * mm});
            skLineSegment(sketch, "E288", {"start": v(160.75, 51.46) * mm, "end": v(161, 51.21) * mm});
            skLineSegment(sketch, "E289", {"start": v(161, 51.21) * mm, "end": v(161.31, 51.05) * mm});
            skLineSegment(sketch, "E290", {"start": v(161.31, 51.05) * mm, "end": v(161.66, 51) * mm});
            skLineSegment(sketch, "E291", {"start": v(161.66, 51) * mm, "end": v(162.01, 51.05) * mm});
            skLineSegment(sketch, "E292", {"start": v(162.01, 51.05) * mm, "end": v(162.33, 51.21) * mm});
            skLineSegment(sketch, "E293", {"start": v(162.33, 51.21) * mm, "end": v(162.58, 51.46) * mm});
            skLineSegment(sketch, "E294", {"start": v(162.58, 51.46) * mm, "end": v(162.74, 51.78) * mm});
            skLineSegment(sketch, "E295", {"start": v(162.74, 51.78) * mm, "end": v(162.8, 52.12) * mm});
            skLineSegment(sketch, "E296", {"start": v(162.8, 52.12) * mm, "end": v(162.74, 52.47) * mm});
            skLineSegment(sketch, "E297", {"start": v(162.74, 52.47) * mm, "end": v(162.58, 52.8) * mm});
            skLineSegment(sketch, "E298", {"start": v(162.58, 52.8) * mm, "end": v(162.33, 53.04) * mm});
            skLineSegment(sketch, "E299", {"start": v(162.33, 53.04) * mm, "end": v(162.01, 53.2) * mm});
            skLineSegment(sketch, "E300", {"start": v(162.01, 53.2) * mm, "end": v(161.66, 53.26) * mm});
            skLineSegment(sketch, "E301", {"start": v(161.66, 53.26) * mm, "end": v(161.31, 53.2) * mm});
            skLineSegment(sketch, "E302", {"start": v(-162.01, 53.2) * mm, "end": v(-162.33, 53.04) * mm});
            skLineSegment(sketch, "E303", {"start": v(-162.33, 53.04) * mm, "end": v(-162.58, 52.8) * mm});
            skLineSegment(sketch, "E304", {"start": v(-162.58, 52.8) * mm, "end": v(-162.74, 52.47) * mm});
            skLineSegment(sketch, "E305", {"start": v(-162.74, 52.47) * mm, "end": v(-162.8, 52.12) * mm});
            skLineSegment(sketch, "E306", {"start": v(-162.8, 52.12) * mm, "end": v(-162.74, 51.78) * mm});
            skLineSegment(sketch, "E307", {"start": v(-162.74, 51.78) * mm, "end": v(-162.58, 51.46) * mm});
            skLineSegment(sketch, "E308", {"start": v(-162.58, 51.46) * mm, "end": v(-162.33, 51.21) * mm});
            skLineSegment(sketch, "E309", {"start": v(-162.33, 51.21) * mm, "end": v(-162.01, 51.05) * mm});
            skLineSegment(sketch, "E310", {"start": v(-162.01, 51.05) * mm, "end": v(-161.66, 51) * mm});
            skLineSegment(sketch, "E311", {"start": v(-161.66, 51) * mm, "end": v(-161.31, 51.05) * mm});
            skLineSegment(sketch, "E312", {"start": v(-161.31, 51.05) * mm, "end": v(-161, 51.21) * mm});
            skLineSegment(sketch, "E313", {"start": v(-161, 51.21) * mm, "end": v(-160.75, 51.46) * mm});
            skLineSegment(sketch, "E314", {"start": v(-160.75, 51.46) * mm, "end": v(-160.59, 51.78) * mm});
            skLineSegment(sketch, "E315", {"start": v(-160.59, 51.78) * mm, "end": v(-160.53, 52.12) * mm});
            skLineSegment(sketch, "E316", {"start": v(-160.53, 52.12) * mm, "end": v(-160.59, 52.47) * mm});
            skLineSegment(sketch, "E317", {"start": v(-160.59, 52.47) * mm, "end": v(-160.75, 52.8) * mm});
            skLineSegment(sketch, "E318", {"start": v(-160.75, 52.8) * mm, "end": v(-161, 53.04) * mm});
            skLineSegment(sketch, "E319", {"start": v(-161, 53.04) * mm, "end": v(-161.31, 53.2) * mm});
            skLineSegment(sketch, "E320", {"start": v(-161.31, 53.2) * mm, "end": v(-161.66, 53.26) * mm});
            skLineSegment(sketch, "E321", {"start": v(-161.66, 53.26) * mm, "end": v(-162.01, 53.2) * mm});
            skSolve(sketch);
        }
        {
            var Q0;
            Q0=qSketchRegion(id+"F0",true);
            extrude(context, id + "F1", {"entities" : qUnion([Q0]), "depth" : 1.25 * mm});
        }
    });
